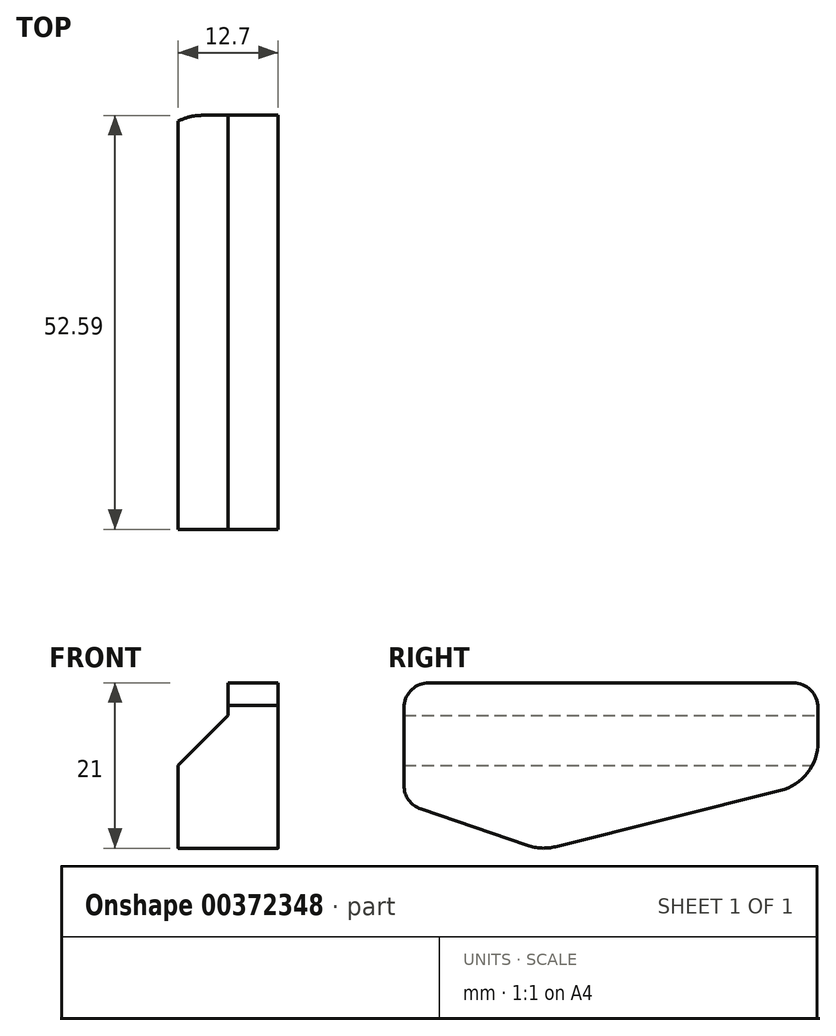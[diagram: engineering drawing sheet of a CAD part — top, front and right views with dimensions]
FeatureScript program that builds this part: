
annotation { "Feature Type Name" : "Feature", "Feature Type Description" : "" }
export const myFeature = defineFeature(function(context is Context, id is Id, definition is map)
    precondition{}
    {
        {
            var Q0;
            Q0=qCreatedBy(makeId("Right.planeOp"),FACE);
            var sketch = newSketch(context, id + "F0", { "sketchPlane" : qUnion([Q0])});
            skLineSegment(sketch, "E0", {"start": v(-21.92, 4.16) * mm, "end": v(24.34, 4.16) * mm});
            skLineSegment(sketch, "E1", {"start": v(27.51, -3.36) * mm, "end": v(27.51, 0.98) * mm});
            skPoint(sketch, "E2.visualSharp", {"position": v(-23.29, 4.16) * mm});
            skArc(sketch, "E2.filletArc", {"start": v(-21.92, 4.16) * mm, "mid": v(-24.06, 3.33) * mm, "end": v(-25.08, 1.28) * mm});
            skPoint(sketch, "E3.visualSharp", {"position": v(-25.08, -20.94) * mm});
            skPoint(sketch, "E4.visualSharp", {"position": v(27.51, -8.54) * mm});
            skArc(sketch, "E4.filletArc", {"start": v(22.7, -9.52) * mm, "mid": v(26.17, -7.27) * mm, "end": v(27.51, -3.36) * mm});
            skPoint(sketch, "E5.visualSharp", {"position": v(27.51, 4.16) * mm});
            skArc(sketch, "E5.filletArc", {"start": v(27.51, 0.98) * mm, "mid": v(26.58, 3.23) * mm, "end": v(24.34, 4.16) * mm});
            skLineSegment(sketch, "E6", {"start": v(-22.93, -11.88) * mm, "end": v(-9.41, -16.5) * mm});
            skLineSegment(sketch, "E7", {"start": v(-25.08, 1.28) * mm, "end": v(-25.08, -8.88) * mm});
            skLineSegment(sketch, "E8", {"start": v(22.7, -9.52) * mm, "end": v(-5.82, -16.65) * mm});
            skPoint(sketch, "E9.visualSharp", {"position": v(-25.08, -11.15) * mm});
            skArc(sketch, "E9.filletArc", {"start": v(-25.08, -8.88) * mm, "mid": v(-24.49, -10.73) * mm, "end": v(-22.93, -11.88) * mm});
            skPoint(sketch, "E10.visualSharp", {"position": v(-7.64, -17.1) * mm});
            skArc(sketch, "E10.filletArc", {"start": v(-9.41, -16.5) * mm, "mid": v(-7.63, -16.84) * mm, "end": v(-5.82, -16.65) * mm});
            skSolve(sketch);
        }
        {
            var Q0;
            Q0 = qSketchRegion(id + "F0", true);
            extrude(context, id + "F1", {"entities" : qUnion([Q0]), "endBound" : BoundingType.SYMMETRIC, "depth" : 12.7 * mm});
        }
        {
            var Q0;
            Q0=qCreatedBy(makeId("Front.planeOp"),FACE);
            var sketch = newSketch(context, id + "F2", { "sketchPlane" : qUnion([Q0])});
            skLineSegment(sketch, "E11", {"start": v(0, 0) * mm, "end": v(-6.35, -6.35) * mm});
            skLineSegment(sketch, "E12", {"start": v(0, 0) * mm, "end": v(0, 6.35) * mm});
            skLineSegment(sketch, "E13", {"start": v(-6.35, -6.35) * mm, "end": v(-12.7, -6.35) * mm});
            skLineSegment(sketch, "E14", {"start": v(-12.7, -6.35) * mm, "end": v(-12.7, 6.35) * mm});
            skLineSegment(sketch, "E15", {"start": v(-12.7, 6.35) * mm, "end": v(0, 6.35) * mm});
            skSolve(sketch);
        }
        {
            var Q0;
            Q0 = qSketchRegion(id + "F2", true);
            extrude(context, id + "F3", {"entities" : qUnion([Q0]), "operationType" : NewBodyOperationType.REMOVE, "endBound" : BoundingType.SYMMETRIC, "depth" : 76.2 * mm});
        }
    });
